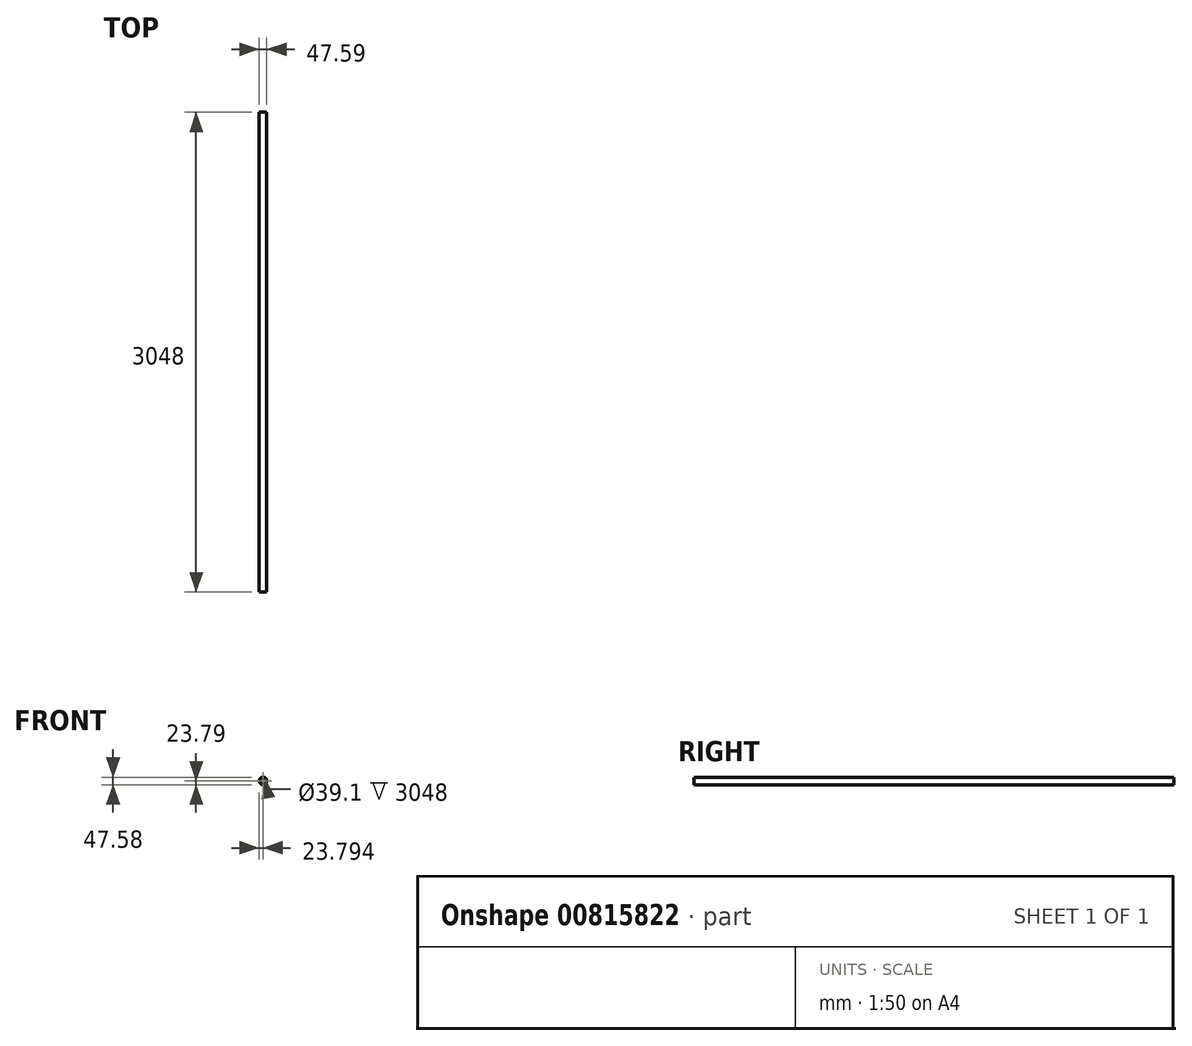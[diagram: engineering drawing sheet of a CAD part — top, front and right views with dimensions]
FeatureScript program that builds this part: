
annotation { "Feature Type Name" : "Feature", "Feature Type Description" : "" }
export const myFeature = defineFeature(function(context is Context, id is Id, definition is map)
    precondition{}
    {
        {
            var Q0;
            Q0=qCreatedBy(makeId("Front.planeOp"),FACE);
            var sketch = newSketch(context, id + "F0", { "sketchPlane" : qUnion([Q0])});
            skCircle(sketch, "E0", {"center": v(-39.85, 0) * mm, "radius": 23.8 * mm});
            skCircle(sketch, "E1", {"center": v(45.53, 0) * mm, "radius": 23.8 * mm});
            skCircle(sketch, "E2", {"center": v(-39.85, 0) * mm, "radius": 19.55 * mm});
            skCircle(sketch, "E3", {"center": v(45.53, 0) * mm, "radius": 19.55 * mm});
            skSolve(sketch);
        }
        {
            var Q0;
            Q0=makeQuery(id+"F0.imprint","IMPRINT",FACE,{"disambiguationData":[TD([[makeQuery(id+"F0.imprint","IMPRINT",EDGE,{"derivedFrom":sQuery(id+"F0.wireOp",EDGE,"E0")}),1.0]])]});
            extrude(context, id + "F1", {"entities" : qUnion([Q0]), "depth" : 3048 * mm, "offsetDistance" : 25.4 * mm});
        }
    });
